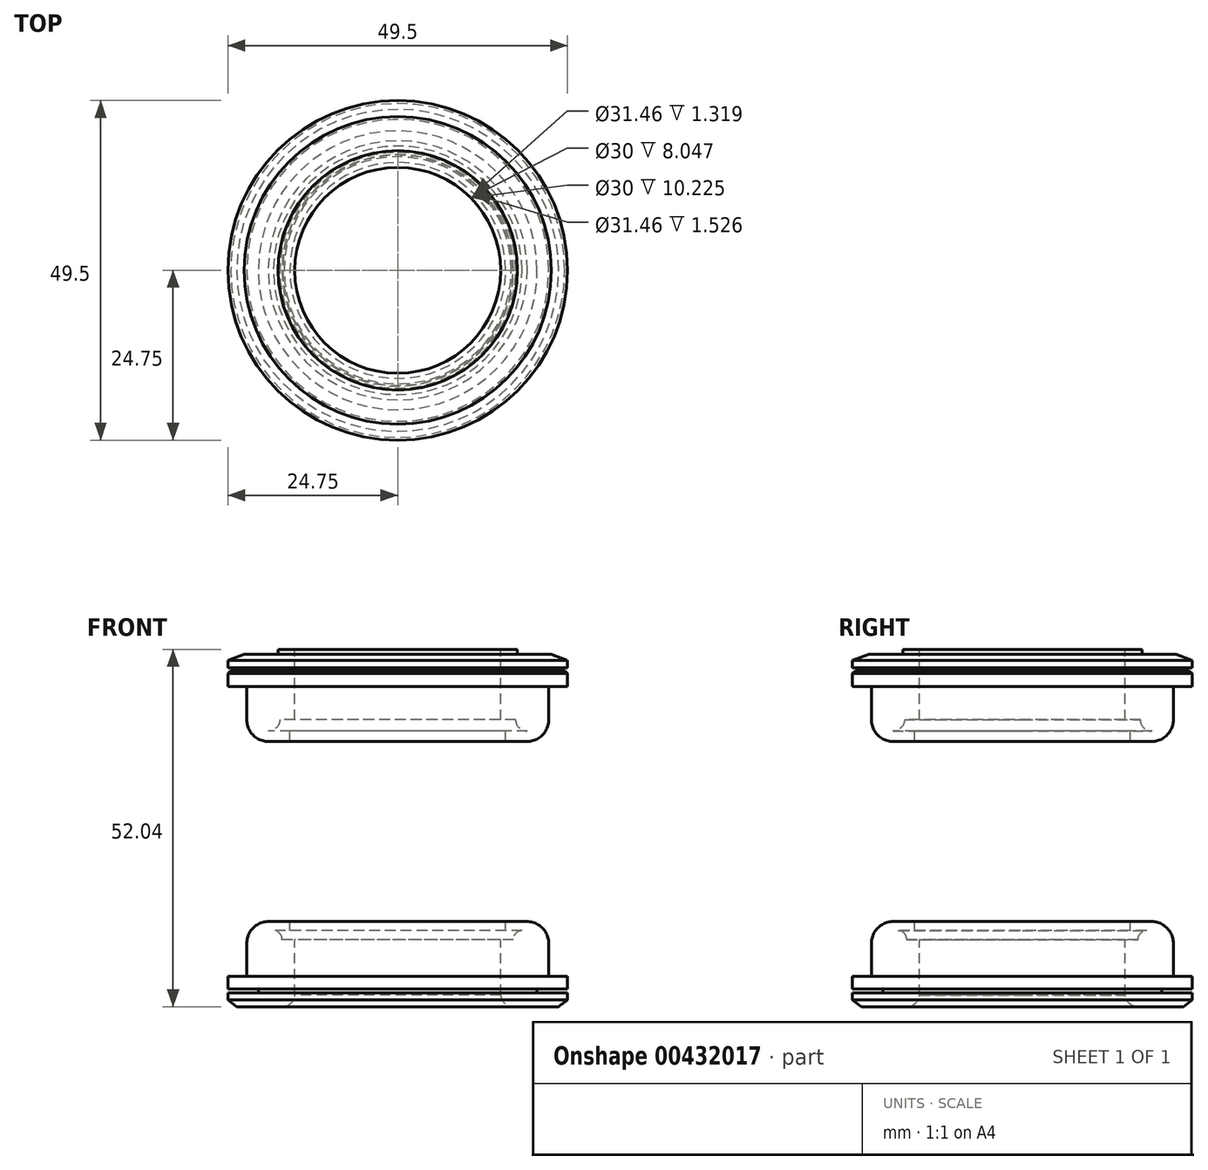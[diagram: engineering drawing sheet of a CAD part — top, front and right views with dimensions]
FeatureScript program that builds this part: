
annotation { "Feature Type Name" : "Feature", "Feature Type Description" : "" }
export const myFeature = defineFeature(function(context is Context, id is Id, definition is map)
    precondition{}
    {
        {
            var Q0;
            Q0=qCreatedBy(makeId("Front.planeOp"),FACE);
            var sketch = newSketch(context, id + "F0", { "sketchPlane" : qUnion([Q0])});
            skLineSegment(sketch, "E0", {"start": v(0, 21.87) * mm, "end": v(0, -31.48) * mm, "construction": true});
            skLineSegment(sketch, "E1", {"start": v(15, 20.28) * mm, "end": v(15, 10.05) * mm});
            skLineSegment(sketch, "E2", {"start": v(15, 20.28) * mm, "end": v(17.44, 20.28) * mm});
            skLineSegment(sketch, "E3", {"start": v(24.75, 18.69) * mm, "end": v(24.75, 17.61) * mm});
            skLineSegment(sketch, "E4", {"start": v(23.46, -31.76) * mm, "end": v(16.58, -31.76) * mm});
            skLineSegment(sketch, "E5", {"start": v(22, -27.36) * mm, "end": v(24.75, -27.36) * mm});
            skLineSegment(sketch, "E6", {"start": v(15.73, -19.36) * mm, "end": v(18.83, -19.36) * mm});
            skLineSegment(sketch, "E7", {"start": v(22, 14.88) * mm, "end": v(24.75, 14.88) * mm});
            skLineSegment(sketch, "E8", {"start": v(15.73, 6.88) * mm, "end": v(18.83, 6.88) * mm});
            skLineSegment(sketch, "E9", {"start": v(22, -22.53) * mm, "end": v(22, -27.36) * mm});
            skLineSegment(sketch, "E10", {"start": v(22, 14.88) * mm, "end": v(22, 10.05) * mm});
            skArc(sketch, "E11.filletArc", {"start": v(22, -22.53) * mm, "mid": v(21.07, -20.29) * mm, "end": v(18.83, -19.36) * mm});
            skLineSegment(sketch, "E12", {"start": v(18.88, 8.4) * mm, "end": v(15.73, 8.4) * mm});
            skLineSegment(sketch, "E13", {"start": v(17.18, 10.05) * mm, "end": v(15, 10.05) * mm});
            skLineSegment(sketch, "E14", {"start": v(19.87, 19.58) * mm, "end": v(22.4, 19.58) * mm});
            skLineSegment(sketch, "E15", {"start": v(22.4, 19.58) * mm, "end": v(24.75, 18.69) * mm});
            skLineSegment(sketch, "E16.trimOffspring", {"start": v(24.75, 16.79) * mm, "end": v(24.75, -29.19) * mm});
            skLineSegment(sketch, "E17", {"start": v(24.33, 17.2) * mm, "end": v(24.75, 16.79) * mm});
            skLineSegment(sketch, "E18", {"start": v(15.73, 8.4) * mm, "end": v(15.73, 6.88) * mm});
            skLineSegment(sketch, "E19", {"start": v(17.44, 20.28) * mm, "end": v(17.44, 19.58) * mm});
            skLineSegment(sketch, "E20", {"start": v(17.44, 19.58) * mm, "end": v(19.87, 19.58) * mm});
            skArc(sketch, "E21", {"start": v(18.83, 6.88) * mm, "mid": v(21.07, 7.8) * mm, "end": v(22, 10.05) * mm});
            skArc(sketch, "E22", {"start": v(17.18, 10.05) * mm, "mid": v(17.7, 8.88) * mm, "end": v(18.88, 8.4) * mm});
            skLineSegment(sketch, "E23", {"start": v(16.58, -31.76) * mm, "end": v(16.55, -31.76) * mm});
            skLineSegment(sketch, "E24", {"start": v(15, -30.05) * mm, "end": v(15, -22) * mm});
            skLineSegment(sketch, "E25", {"start": v(24.33, 17.2) * mm, "end": v(22, 17.2) * mm});
            skLineSegment(sketch, "E26", {"start": v(22, 17.2) * mm, "end": v(22, 17.61) * mm});
            skLineSegment(sketch, "E27", {"start": v(22, 17.61) * mm, "end": v(24.75, 17.61) * mm});
            skLineSegment(sketch, "E28", {"start": v(15.73, -20.68) * mm, "end": v(18.12, -20.68) * mm});
            skLineSegment(sketch, "E29", {"start": v(15.73, -19.36) * mm, "end": v(15.73, -20.68) * mm});
            skArc(sketch, "E30", {"start": v(15, -30.05) * mm, "mid": v(15.47, -31.18) * mm, "end": v(16.55, -31.76) * mm});
            skLineSegment(sketch, "E31", {"start": v(24.75, -30.76) * mm, "end": v(23.46, -31.76) * mm});
            skLineSegment(sketch, "E32", {"start": v(24.75, -29.78) * mm, "end": v(20.32, -29.78) * mm});
            skLineSegment(sketch, "E33", {"start": v(20.32, -29.78) * mm, "end": v(20.32, -29.19) * mm});
            skLineSegment(sketch, "E34", {"start": v(20.32, -29.19) * mm, "end": v(24.75, -29.19) * mm});
            skLineSegment(sketch, "E35.trimOffspring", {"start": v(24.75, -29.78) * mm, "end": v(24.75, -30.76) * mm});
            skLineSegment(sketch, "E36", {"start": v(15, -22) * mm, "end": v(16.86, -22) * mm});
            skArc(sketch, "E37", {"start": v(18.12, -20.68) * mm, "mid": v(17.2, -21.07) * mm, "end": v(16.86, -22) * mm});
            skSolve(sketch);
        }
        {
            var Q0;
            Q0=makeQuery(id+"F0.imprint","IMPRINT",FACE,{"disambiguationData":[TD([[makeQuery(id+"F0.imprint","IMPRINT",EDGE,{"derivedFrom":sQuery(id+"F0.wireOp",EDGE,"E1")}),1.0]])]});
            var Q1;
            Q1=sQuery(id+"F0.wireOp",EDGE,"E0");
            revolve(context, id + "F1", {"entities" : qUnion([Q0]), "axis" : qUnion([Q1]), "revolveType" : RevolveType.FULL});
        }
        {
            var Q0;
            Q0=makeQuery(id+"F0.imprint","IMPRINT",FACE,{"disambiguationData":[TD([[makeQuery(id+"F0.imprint","IMPRINT",EDGE,{"derivedFrom":sQuery(id+"F0.wireOp",EDGE,"E4")}),-1.0]])]});
            var Q1;
            Q1=sQuery(id+"F0.wireOp",EDGE,"E0");
            revolve(context, id + "F2", {"entities" : qUnion([Q0]), "axis" : qUnion([Q1]), "revolveType" : RevolveType.FULL});
        }
    });
